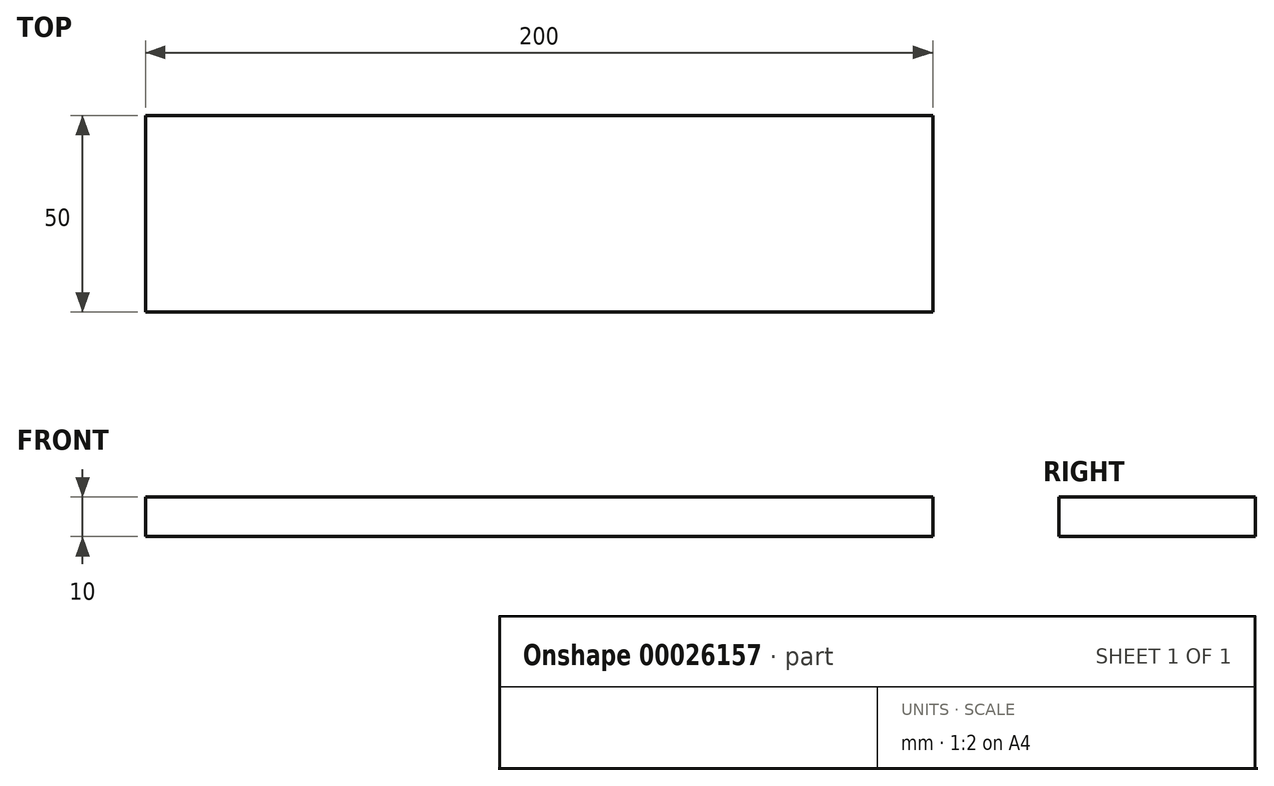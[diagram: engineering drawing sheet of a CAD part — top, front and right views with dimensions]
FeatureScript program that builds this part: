
annotation { "Feature Type Name" : "Feature", "Feature Type Description" : "" }
export const myFeature = defineFeature(function(context is Context, id is Id, definition is map)
    precondition{}
    {
        {
            var Q0;
            Q0=qCreatedBy(makeId("Top.planeOp"),FACE);
            var sketch = newSketch(context, id + "F0", { "sketchPlane" : qUnion([Q0])});
            skLineSegment(sketch, "E0.bottom", {"start": v(-6.9, -97) * mm, "end": v(-206.9, -97) * mm});
            skLineSegment(sketch, "E0.top", {"start": v(-6.9, -47) * mm, "end": v(-206.9, -47) * mm});
            skLineSegment(sketch, "E0.left", {"start": v(-6.9, -97) * mm, "end": v(-6.9, -47) * mm});
            skLineSegment(sketch, "E0.right", {"start": v(-206.9, -97) * mm, "end": v(-206.9, -47) * mm});
            skSolve(sketch);
        }
        {
            var Q0;
            Q0=makeQuery(id+"F0.imprint","IMPRINT",FACE,{"disambiguationData":[TD([[makeQuery(id+"F0.imprint","IMPRINT",EDGE,{"derivedFrom":sQuery(id+"F0.wireOp",EDGE,"E0.bottom")}),-1.0]])]});
            extrude(context, id + "F1", {"entities" : qUnion([Q0]), "depth" : 10 * mm});
        }
    });
